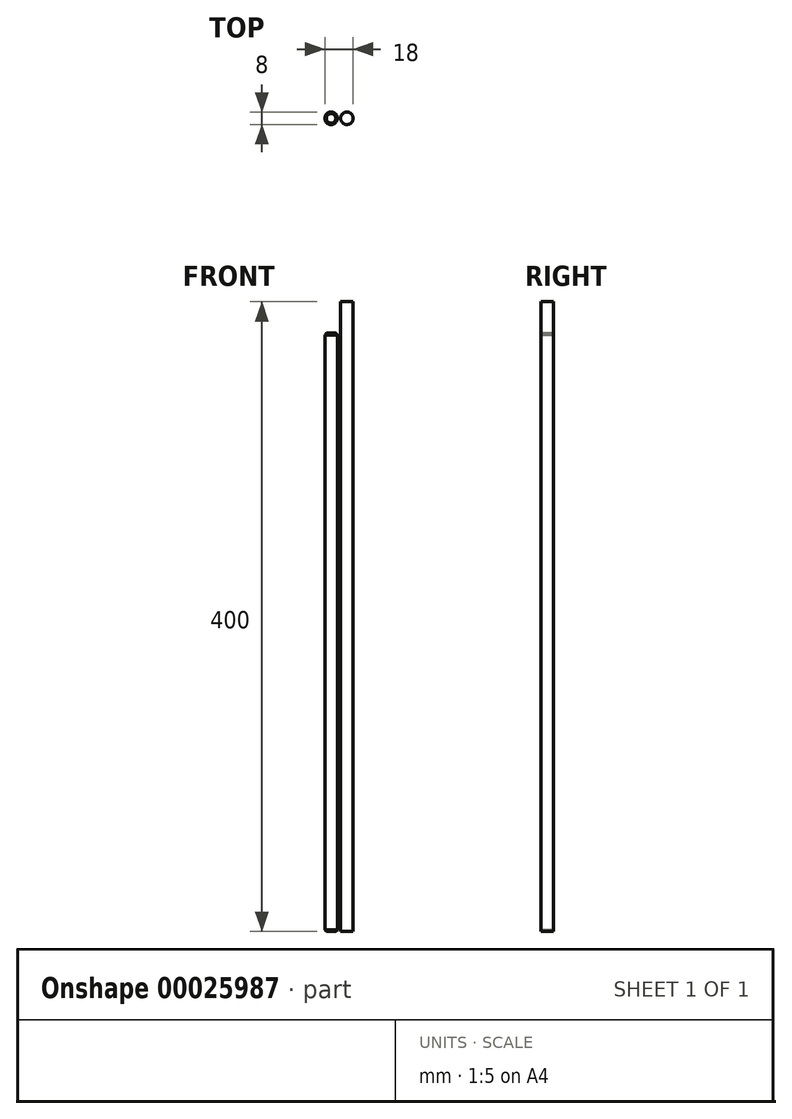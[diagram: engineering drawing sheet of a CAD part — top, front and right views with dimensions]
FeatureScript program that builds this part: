
annotation { "Feature Type Name" : "Feature", "Feature Type Description" : "" }
export const myFeature = defineFeature(function(context is Context, id is Id, definition is map)
    precondition{}
    {
        {
            var Q0;
            Q0=qCreatedBy(makeId("Top.planeOp"),FACE);
            var sketch = newSketch(context, id + "F0", { "sketchPlane" : qUnion([Q0])});
            skCircle(sketch, "E0", {"center": v(0, 0) * mm, "radius": 4 * mm});
            skSolve(sketch);
        }
        {
            var Q0;
            Q0=makeQuery(id+"F0.imprint","IMPRINT",FACE,{"disambiguationData":[TD([[makeQuery(id+"F0.imprint","IMPRINT",EDGE,{"derivedFrom":sQuery(id+"F0.wireOp",EDGE,"E0")}),1.0]])]});
            extrude(context, id + "F1", {"entities" : qUnion([Q0]), "depth" : 380 * mm});
        }
        {
            var Q0;
            Q0=makeQuery(id+"F1.opExtrude","CAP_EDGE",EDGE,{"disambiguationData":[OSD([sQuery(id+"F0.wireOp",EDGE,"E0")])],"isStart":true});
            var Q1;
            Q1=makeQuery(id+"F1.opExtrude","CAP_EDGE",EDGE,{"disambiguationData":[OSD([sQuery(id+"F0.wireOp",EDGE,"E0")])],"isStart":false});
            chamfer(context, id + "F2", {"entities" : qUnion([Q0, Q1]), "width" : 1 * mm, "tangentPropagation" : true});
        }
        {
            var Q0;
            Q0=qCreatedBy(makeId("Top.planeOp"),FACE);
            var sketch = newSketch(context, id + "F3", { "sketchPlane" : qUnion([Q0])});
            skCircle(sketch, "E1", {"center": v(10, 0) * mm, "radius": 4 * mm});
            skSolve(sketch);
        }
        {
            var Q0;
            Q0=makeQuery(id+"F3.imprint","IMPRINT",FACE,{"disambiguationData":[TD([[makeQuery(id+"F3.imprint","IMPRINT",EDGE,{"derivedFrom":sQuery(id+"F3.wireOp",EDGE,"E1")}),1.0]])]});
            extrude(context, id + "F4", {"entities" : qUnion([Q0]), "depth" : 400 * mm});
        }
    });
